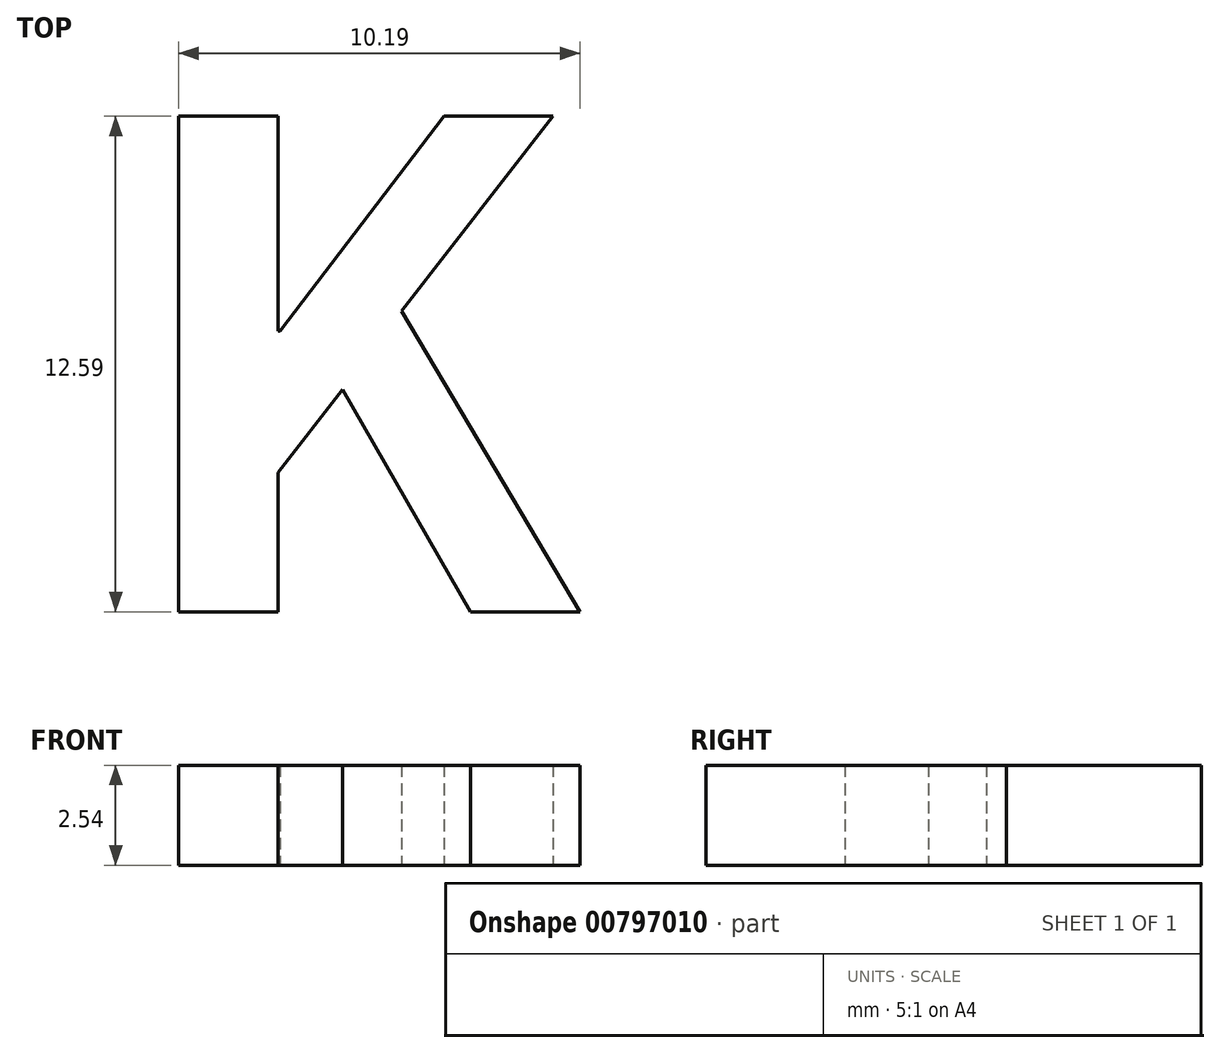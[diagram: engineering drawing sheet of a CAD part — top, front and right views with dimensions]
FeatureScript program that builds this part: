
annotation { "Feature Type Name" : "Feature", "Feature Type Description" : "" }
export const myFeature = defineFeature(function(context is Context, id is Id, definition is map)
    precondition{}
    {
        {
            var Q0;
            Q0=qCreatedBy(makeId("Top.planeOp"),FACE);
            var sketch = newSketch(context, id + "F0", { "sketchPlane" : qUnion([Q0])});
            skText(sketch, "E0", { "text": "K", "fontName": "NotoSansCJKtc-Bold.otf"});
            const initialGuessF0  = {"E0": [-0.00533, -0.00739, 1, 0, 0.01225]};
            skSetInitialGuess(sketch, initialGuessF0);
            skSolve(sketch);
        }
        {
            var Q0;
            Q0 = qSketchRegion(id + "F0", true);
            extrude(context, id + "F1", {"entities" : qUnion([Q0]), "depth" : 2.54 * mm, "offsetDistance" : 25.4 * mm});
        }
    });
